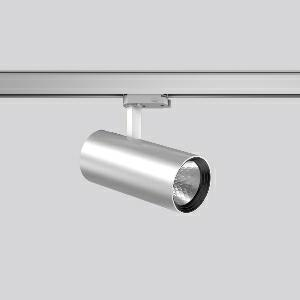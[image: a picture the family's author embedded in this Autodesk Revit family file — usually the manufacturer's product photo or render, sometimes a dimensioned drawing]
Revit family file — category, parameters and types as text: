
# Revit family: deecos_s_mini_742193_004_1_8ca0
name_source: partatom
category: Lighting Fixtures
units: mm (PartAtom-declared; Revit-internal decimal feet)

## family parameters
Cut with Voids When Loaded = No
Host = Face
Light Source = No
Part Type = Normal
Room Calculation Point = No
Round Connector Dimension = Use Diameter
Shared = No

## types (1)
- DEECOS S mini (1 x LED Modul 940, 2500 lm, 4000)
    Apparent Load = 22 VA
    Approval mark = CE
    CIE Flux Codes = 100 100 100 100 100
    Color Rendering = 92
    Color Temperature = 4000
    Default Elevation = 1800 mm
    Description = Series: DEECOS S mini
LED surface-mounted projector in modern design with no visible cooling ribs. Housing: die-cast aluminium, powder-coated. Rotation range: 356°. Swivel range: 90°. Black plastic ring and recessed LED to prevent glare from the side. Optical assembly with reflector made of MIRO-Silver with 98% total light reflection for outstanding efficiency - can be changed without tools. Best colour rendering index Ra>90. Superspot version with small spot LED. With multi adaptor for 3-circuit tracks 230 V. Suitable for Track on ceiling, Wall track. High quality converter without flickering and stroboscopic effect. The following accessories can be mounted without use of tools: interchangeable lenses, decorative glasses, honeycomb louvre, clear and frosted diffusers, white interchangeable plastic ring. 
Colour: silver
Diameter: 87 mm
Height: 214 mm
Lamp: LED
Socket: without socket
Colour temperature: 4000K
Colour rendering index (CRI): 92
System power: 22 W
Rated luminous flux: 2500 lm
Luminous efficiency: 114 lm/W
Control gear: Regulated power supply
Protection class: I
Type of protection: IP 20
    Height = 214 mm
    Lamp = 1 x LED Modul 940
    Lamp Light Flux = 2500 lm
    Lamp count = 1
    Length = 87 mm
    Lifetime = 50000 h
    Luminous efficacy = 114 lm/W
    Manufacturer = RZB
    ModVariant = No
    Model = 742193.004.1
    Mounting Place = Ceiling
    Mounting Type = Rail mounted
    Number of Poles = 1
    OnlyDefault = Yes
    Power Factor = 1
    Product Name = DEECOS S mini
    Product group = Track mounted projectors
    ProductGroupID = 301
    Protection Class = Protection class I
    Protection Degree = IP 20
    RLX_Detail_Level = 1
    RLX_Emergency_Light_Flux = 0 lm
    RLX_Emergency_Type = 0
    RLX_Emergency_Type_DB = No
    RlxData = <blob elided: 37513 chars, md5=cc84c119>
    Socket = socket
    Standby Power = 0 W
    System Light Flux = 2500 lm
    System Power = 22 W
    Type Comments = Product without accessories
    Type Image = 741926.004.jpg
    URL = http://relux.com
    VarID = ---
    Voltage = 230 V
    Voltage Range = 220-240 V
    Weight = 0.00 kg
    Width = 0 mm  [stored 0 ft]

note: [stored X ft] marks values corroborated as IEEE doubles in the binary element streams (Revit-internal decimal feet)

## geometry (parser evidence)
native form markers: Blend x4, Sweep x14
no freeform markers — native parametric forms only
